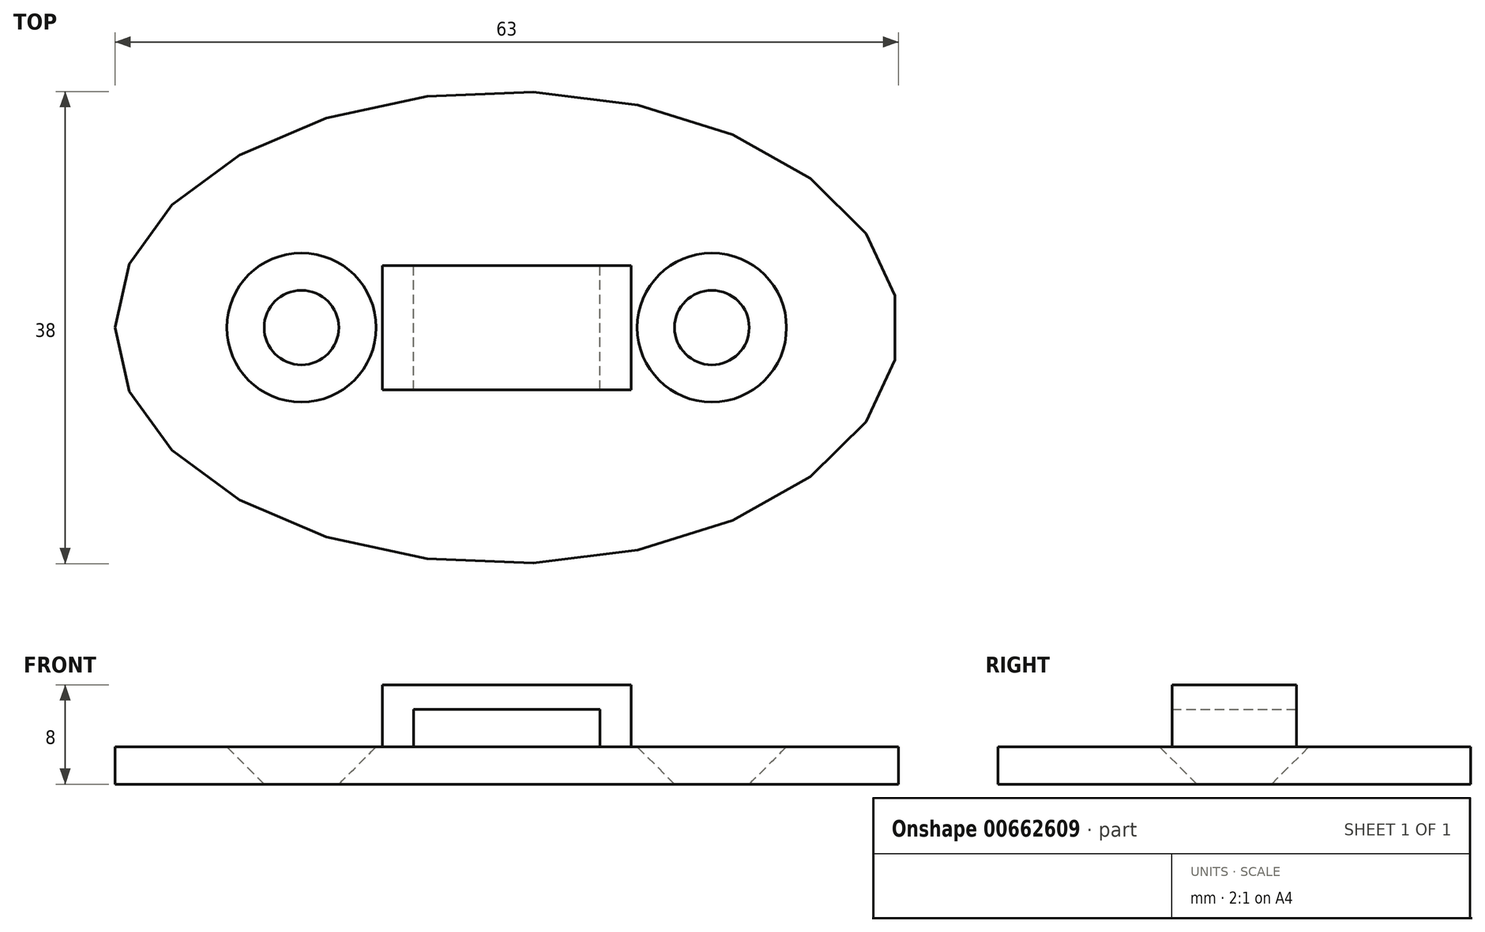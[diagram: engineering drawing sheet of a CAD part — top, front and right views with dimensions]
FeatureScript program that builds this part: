
annotation { "Feature Type Name" : "Feature", "Feature Type Description" : "" }
export const myFeature = defineFeature(function(context is Context, id is Id, definition is map)
    precondition{}
    {
        {
            var Q0;
            Q0=qCreatedBy(makeId("Top.planeOp"),FACE);
            var sketch = newSketch(context, id + "F0", { "sketchPlane" : qUnion([Q0])});
            skCircle(sketch, "E0", {"center": v(-16.5, 0) * mm, "radius": 3 * mm});
            skCircle(sketch, "E1", {"center": v(16.5, 0) * mm, "radius": 3 * mm});
            skEllipse(sketch, "E2", {"center": v(0, 0) * mm, "majorRadius": 31.5 * mm, "minorRadius": 19 * mm, "majorAxis": v(-1, 0)});
            skSolve(sketch);
        }
        {
            var Q0;
            Q0=makeQuery(id+"F0.imprint","IMPRINT",FACE,{"disambiguationData":[TD([[makeQuery(id+"F0.imprint","IMPRINT",EDGE,{"derivedFrom":sQuery(id+"F0.wireOp",EDGE,"E0")}),-1.0]])]});
            extrude(context, id + "F1", {"entities" : qUnion([Q0]), "depth" : 3 * mm, "offsetDistance" : 25 * mm});
        }
        {
            var Q0;
            Q0=qCreatedBy(makeId("Front.planeOp"),FACE);
            var sketch = newSketch(context, id + "F2", { "sketchPlane" : qUnion([Q0])});
            skLineSegment(sketch, "E3.0", {"start": v(10, 3) * mm, "end": v(7.5, 3) * mm});
            skLineSegment(sketch, "E4", {"start": v(-10, 3) * mm, "end": v(-10, 8) * mm});
            skLineSegment(sketch, "E5", {"start": v(-10, 8) * mm, "end": v(10, 8) * mm});
            skLineSegment(sketch, "E6", {"start": v(10, 8) * mm, "end": v(10, 3) * mm});
            skLineSegment(sketch, "E7", {"start": v(-7.5, 3) * mm, "end": v(-7.5, 6.01) * mm});
            skLineSegment(sketch, "E8", {"start": v(-7.5, 6.01) * mm, "end": v(7.5, 6.01) * mm});
            skLineSegment(sketch, "E9", {"start": v(7.5, 6.01) * mm, "end": v(7.5, 3) * mm});
            skPoint(sketch, "E10.orphan", {"position": v(-31.5, 3) * mm});
            skPoint(sketch, "E11.orphan", {"position": v(31.5, 3) * mm});
            skLineSegment(sketch, "E12.trimOffspring", {"start": v(-7.5, 3) * mm, "end": v(-10, 3) * mm});
            skSolve(sketch);
        }
        {
            var Q0;
            Q0 = qSketchRegion(id + "F2", true);
            extrude(context, id + "F3", {"entities" : qUnion([Q0]), "operationType" : NewBodyOperationType.ADD, "endBound" : BoundingType.SYMMETRIC, "depth" : 10 * mm, "offsetDistance" : 25 * mm});
        }
        {
            var Q0;
            Q0=makeQuery(id+"F1.opExtrude","CAP_EDGE",EDGE,{"disambiguationData":[OSD([sQuery(id+"F0.wireOp",EDGE,"E0")])],"isStart":false});
            var Q1;
            Q1=makeQuery(id+"F1.opExtrude","CAP_EDGE",EDGE,{"disambiguationData":[OSD([sQuery(id+"F0.wireOp",EDGE,"E1")])],"isStart":false});
            chamfer(context, id + "F4", {"entities" : qUnion([Q0, Q1]), "width" : 3 * mm, "tangentPropagation" : true});
        }
    });
